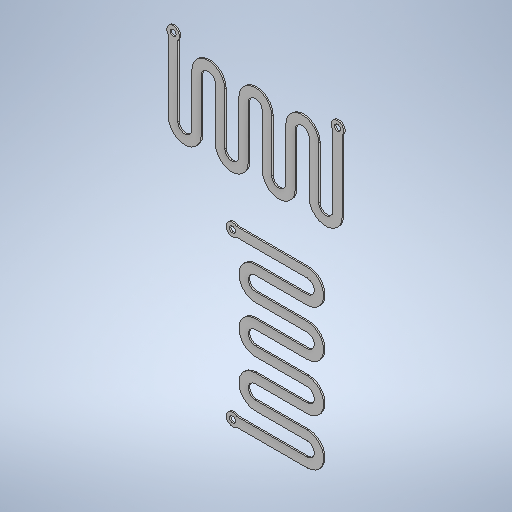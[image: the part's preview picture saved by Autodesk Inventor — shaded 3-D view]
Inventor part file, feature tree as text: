
AUTODESK INVENTOR PART (.ipt)
format: ipt  version: 2025.2 (Build 292293000, 293)  size: 370,176 bytes
history: native  units: mm
features: other x1, extrude x1, sketch x1
ambient origin geometry x8: Origin, YZ Plane, XZ Plane, XY Plane, X Axis, Y Axis, Z Axis, Center Point
bodies: Body1 (feature_tree)
feature tree (3):
  other  "Sólido1"
  extrude  "Extrusão1"  Depth=300.0mm
  sketch  "Esboço1"  dims[d0=10000.0mm d1=17500.0mm d2=2700.0mm d5=15000.0mm d7=3000.0mm d8=2000.0mm d12=1300.0mm d13=300.0mm d14=0.0mm]
